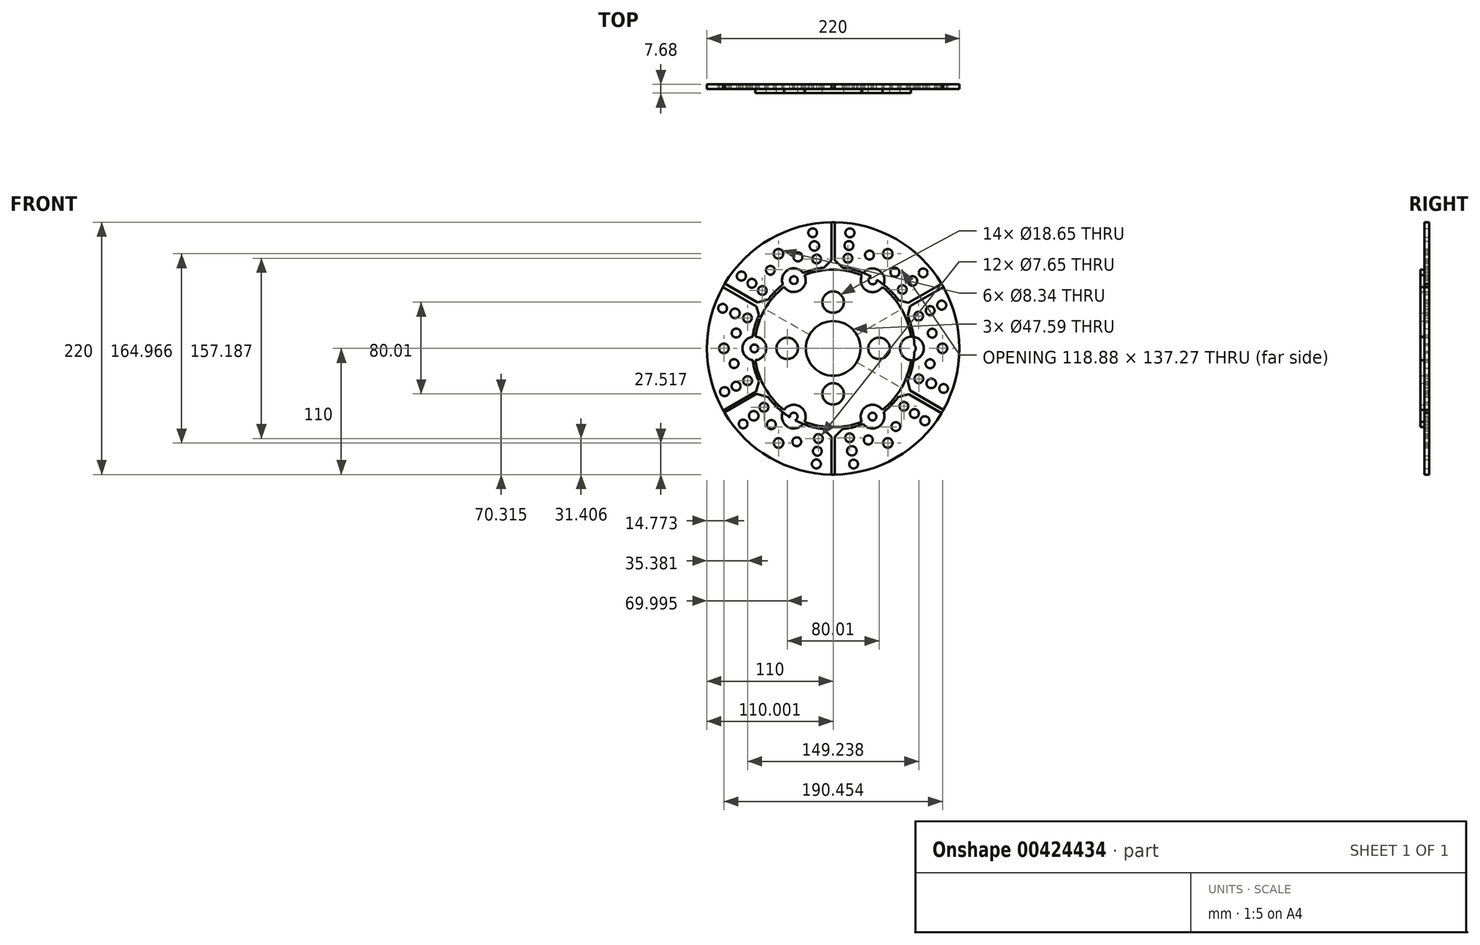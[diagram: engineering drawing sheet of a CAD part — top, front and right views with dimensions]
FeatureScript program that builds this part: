
annotation { "Feature Type Name" : "Feature", "Feature Type Description" : "" }
export const myFeature = defineFeature(function(context is Context, id is Id, definition is map)
    precondition{}
    {
        {
            var Q0;
            Q0=qCreatedBy(makeId("Front.planeOp"),FACE);
            var sketch = newSketch(context, id + "F0", { "sketchPlane" : qUnion([Q0])});
            skCircle(sketch, "E0", {"center": v(0, 0) * mm, "radius": 110 * mm});
            skLineSegment(sketch, "E1", {"start": v(0, 0) * mm, "end": v(0, -110) * mm});
            skLineSegment(sketch, "E2", {"start": v(0, 0) * mm, "end": v(0, 110) * mm});
            skLineSegment(sketch, "E3", {"start": v(0, 0) * mm, "end": v(95.26, 55) * mm});
            skLineSegment(sketch, "E4", {"start": v(0, 0) * mm, "end": v(95.27, -55) * mm});
            skLineSegment(sketch, "E5", {"start": v(0, 0) * mm, "end": v(-95.26, 55) * mm});
            skLineSegment(sketch, "E6", {"start": v(0, 0) * mm, "end": v(-95.26, -55) * mm});
            skCircle(sketch, "E7", {"center": v(0, 0) * mm, "radius": 68.64 * mm});
            skLineSegment(sketch, "E8", {"start": v(-10.54, 67.82) * mm, "end": v(0, 78.36) * mm});
            skLineSegment(sketch, "E9", {"start": v(0, 78.36) * mm, "end": v(10.54, 67.82) * mm});
            skLineSegment(sketch, "E10", {"start": v(10.7, -67.8) * mm, "end": v(-0.08, -78.58) * mm});
            skLineSegment(sketch, "E11", {"start": v(-0.08, -78.58) * mm, "end": v(-10.9, -67.77) * mm});
            skLineSegment(sketch, "E12", {"start": v(53.47, 43.04) * mm, "end": v(67.87, 39.18) * mm});
            skLineSegment(sketch, "E13", {"start": v(67.87, 39.18) * mm, "end": v(64, 24.78) * mm});
            skLineSegment(sketch, "E14", {"start": v(63.9, -25.04) * mm, "end": v(67.76, -39.44) * mm});
            skLineSegment(sketch, "E15", {"start": v(67.76, -39.44) * mm, "end": v(53.36, -43.3) * mm});
            skLineSegment(sketch, "E16", {"start": v(-53.24, -43.32) * mm, "end": v(-67.64, -39.46) * mm});
            skLineSegment(sketch, "E17", {"start": v(-67.64, -39.46) * mm, "end": v(-63.78, -25.06) * mm});
            skLineSegment(sketch, "E18", {"start": v(-63.8, 25.32) * mm, "end": v(-67.65, 39.72) * mm});
            skLineSegment(sketch, "E19", {"start": v(-67.65, 39.72) * mm, "end": v(-53.25, 43.58) * mm});
            skCircle(sketch, "E20", {"center": v(34.43, 59.38) * mm, "radius": 10.31 * mm});
            skCircle(sketch, "E21", {"center": v(-34.23, 59.49) * mm, "radius": 10.31 * mm});
            skCircle(sketch, "E22", {"center": v(68.64, 0) * mm, "radius": 10.31 * mm});
            skCircle(sketch, "E23", {"center": v(-68.64, 0) * mm, "radius": 10.31 * mm});
            skCircle(sketch, "E24", {"center": v(-34.32, -59.44) * mm, "radius": 10.31 * mm});
            skCircle(sketch, "E25", {"center": v(34.32, -59.44) * mm, "radius": 10.31 * mm});
            skLineSegment(sketch, "E26", {"start": v(-1.37, 110) * mm, "end": v(-1.37, 77) * mm});
            skLineSegment(sketch, "E27", {"start": v(1.46, 110) * mm, "end": v(1.46, 76.9) * mm});
            skLineSegment(sketch, "E28", {"start": v(96.08, 53.56) * mm, "end": v(67.26, 36.92) * mm});
            skLineSegment(sketch, "E29", {"start": v(94.44, 56.4) * mm, "end": v(65.65, 39.77) * mm});
            skLineSegment(sketch, "E30", {"start": v(94.47, -56.35) * mm, "end": v(66, -39.91) * mm});
            skLineSegment(sketch, "E31", {"start": v(96.12, -53.5) * mm, "end": v(67.03, -36.7) * mm});
            skLineSegment(sketch, "E32", {"start": v(-1.44, -77.22) * mm, "end": v(-1.44, -110) * mm});
            skLineSegment(sketch, "E33", {"start": v(1.34, -77.16) * mm, "end": v(1.34, -110) * mm});
            skLineSegment(sketch, "E34", {"start": v(-95.7, -54.25) * mm, "end": v(-67.2, -37.79) * mm});
            skLineSegment(sketch, "E35", {"start": v(-94.77, -55.84) * mm, "end": v(-66.8, -39.69) * mm});
            skLineSegment(sketch, "E36", {"start": v(-96.07, 53.58) * mm, "end": v(-66.84, 36.7) * mm});
            skLineSegment(sketch, "E37", {"start": v(-94.38, 56.5) * mm, "end": v(-66.05, 40.15) * mm});
            skCircle(sketch, "E38", {"center": v(0, 40.32) * mm, "radius": 9.33 * mm});
            skCircle(sketch, "E39", {"center": v(0, -39.69) * mm, "radius": 9.33 * mm});
            skCircle(sketch, "E40", {"center": v(40, 0) * mm, "radius": 9.33 * mm});
            skCircle(sketch, "E41", {"center": v(-40, 0) * mm, "radius": 9.33 * mm});
            skCircle(sketch, "E42", {"center": v(0, 0) * mm, "radius": 70.86 * mm});
            skCircle(sketch, "E43", {"center": v(0, 0) * mm, "radius": 23.8 * mm});
            skCircle(sketch, "E44", {"center": v(-34.23, 59.49) * mm, "radius": 3.38 * mm});
            skCircle(sketch, "E45", {"center": v(34.43, 59.38) * mm, "radius": 3.55 * mm});
            skCircle(sketch, "E46", {"center": v(68.64, 0) * mm, "radius": 3.38 * mm});
            skCircle(sketch, "E47", {"center": v(-34.32, -59.44) * mm, "radius": 3.38 * mm});
            skCircle(sketch, "E48", {"center": v(-68.64, 0) * mm, "radius": 3.38 * mm});
            skCircle(sketch, "E49", {"center": v(34.32, -59.44) * mm, "radius": 3.38 * mm});
            skCircle(sketch, "E50", {"center": v(-79.94, 63.04) * mm, "radius": 3.93 * mm});
            skCircle(sketch, "E51", {"center": v(-70.79, 56.73) * mm, "radius": 3.86 * mm});
            skCircle(sketch, "E52", {"center": v(-61.64, 50.43) * mm, "radius": 3.82 * mm});
            skCircle(sketch, "E53", {"center": v(-14.33, 77.89) * mm, "radius": 3.82 * mm});
            skCircle(sketch, "E54", {"center": v(-16.3, 89.3) * mm, "radius": 4.14 * mm});
            skCircle(sketch, "E55", {"center": v(-17.83, 100.85) * mm, "radius": 3.82 * mm});
            skCircle(sketch, "E56", {"center": v(-47.64, 82.46) * mm, "radius": 4.17 * mm});
            skCircle(sketch, "E57", {"center": v(-30.62, 79.8) * mm, "radius": 3.9 * mm});
            skCircle(sketch, "E58", {"center": v(-54.64, 68.13) * mm, "radius": 3.85 * mm});
            skCircle(sketch, "E59.1.0", {"center": v(-74.62, 26.53) * mm, "radius": 3.82 * mm});
            skCircle(sketch, "E59.1.1", {"center": v(-85.48, 30.53) * mm, "radius": 4.14 * mm});
            skCircle(sketch, "E59.1.2", {"center": v(-84.42, 13.38) * mm, "radius": 3.9 * mm});
            skCircle(sketch, "E59.1.3", {"center": v(-84.53, -32.94) * mm, "radius": 3.86 * mm});
            skCircle(sketch, "E59.1.4", {"center": v(-74.49, -28.17) * mm, "radius": 3.82 * mm});
            skCircle(sketch, "E59.1.5", {"center": v(-95.23, -0.03) * mm, "radius": 4.17 * mm});
            skCircle(sketch, "E59.1.6", {"center": v(-96.25, 34.98) * mm, "radius": 3.82 * mm});
            skCircle(sketch, "E59.1.7", {"center": v(-94.57, -37.7) * mm, "radius": 3.93 * mm});
            skCircle(sketch, "E59.1.8", {"center": v(-86.32, -13.25) * mm, "radius": 3.85 * mm});
            skCircle(sketch, "E59.2.0", {"center": v(-60.28, -51.36) * mm, "radius": 3.82 * mm});
            skCircle(sketch, "E59.2.1", {"center": v(-69.18, -58.76) * mm, "radius": 4.14 * mm});
            skCircle(sketch, "E59.2.2", {"center": v(-53.8, -66.42) * mm, "radius": 3.9 * mm});
            skCircle(sketch, "E59.2.3", {"center": v(-13.74, -89.67) * mm, "radius": 3.86 * mm});
            skCircle(sketch, "E59.2.4", {"center": v(-12.85, -78.6) * mm, "radius": 3.82 * mm});
            skCircle(sketch, "E59.2.5", {"center": v(-47.59, -82.48) * mm, "radius": 4.17 * mm});
            skCircle(sketch, "E59.2.6", {"center": v(-78.42, -65.87) * mm, "radius": 3.82 * mm});
            skCircle(sketch, "E59.2.7", {"center": v(-14.63, -100.75) * mm, "radius": 3.93 * mm});
            skCircle(sketch, "E59.2.8", {"center": v(-31.69, -81.38) * mm, "radius": 3.85 * mm});
            skCircle(sketch, "E59.3.0", {"center": v(14.33, -77.89) * mm, "radius": 3.82 * mm});
            skCircle(sketch, "E59.3.1", {"center": v(16.3, -89.3) * mm, "radius": 4.14 * mm});
            skCircle(sketch, "E59.3.2", {"center": v(30.62, -79.8) * mm, "radius": 3.9 * mm});
            skCircle(sketch, "E59.3.3", {"center": v(70.79, -56.73) * mm, "radius": 3.86 * mm});
            skCircle(sketch, "E59.3.4", {"center": v(61.64, -50.43) * mm, "radius": 3.82 * mm});
            skCircle(sketch, "E59.3.5", {"center": v(47.64, -82.46) * mm, "radius": 4.17 * mm});
            skCircle(sketch, "E59.3.6", {"center": v(17.83, -100.85) * mm, "radius": 3.82 * mm});
            skCircle(sketch, "E59.3.7", {"center": v(79.94, -63.04) * mm, "radius": 3.93 * mm});
            skCircle(sketch, "E59.3.8", {"center": v(54.64, -68.13) * mm, "radius": 3.85 * mm});
            skCircle(sketch, "E59.4.0", {"center": v(74.62, -26.53) * mm, "radius": 3.82 * mm});
            skCircle(sketch, "E59.4.1", {"center": v(85.48, -30.53) * mm, "radius": 4.14 * mm});
            skCircle(sketch, "E59.4.2", {"center": v(84.42, -13.38) * mm, "radius": 3.9 * mm});
            skCircle(sketch, "E59.4.3", {"center": v(84.53, 32.94) * mm, "radius": 3.86 * mm});
            skCircle(sketch, "E59.4.4", {"center": v(74.49, 28.17) * mm, "radius": 3.82 * mm});
            skCircle(sketch, "E59.4.5", {"center": v(95.23, 0.03) * mm, "radius": 4.17 * mm});
            skCircle(sketch, "E59.4.6", {"center": v(96.25, -34.98) * mm, "radius": 3.82 * mm});
            skCircle(sketch, "E59.4.7", {"center": v(94.57, 37.7) * mm, "radius": 3.93 * mm});
            skCircle(sketch, "E59.4.8", {"center": v(86.32, 13.25) * mm, "radius": 3.85 * mm});
            skCircle(sketch, "E59.5.0", {"center": v(60.28, 51.36) * mm, "radius": 3.82 * mm});
            skCircle(sketch, "E59.5.1", {"center": v(69.18, 58.76) * mm, "radius": 4.14 * mm});
            skCircle(sketch, "E59.5.2", {"center": v(53.8, 66.42) * mm, "radius": 3.9 * mm});
            skCircle(sketch, "E59.5.3", {"center": v(13.74, 89.67) * mm, "radius": 3.86 * mm});
            skCircle(sketch, "E59.5.4", {"center": v(12.85, 78.6) * mm, "radius": 3.82 * mm});
            skCircle(sketch, "E59.5.5", {"center": v(47.59, 82.48) * mm, "radius": 4.17 * mm});
            skCircle(sketch, "E59.5.6", {"center": v(78.42, 65.87) * mm, "radius": 3.82 * mm});
            skCircle(sketch, "E59.5.7", {"center": v(14.63, 100.75) * mm, "radius": 3.93 * mm});
            skCircle(sketch, "E59.5.8", {"center": v(31.69, 81.38) * mm, "radius": 3.85 * mm});
            skSolve(sketch);
        }
        {
            var Q0;
            {var subQ9=sQuery(id+"F0.wireOp",EDGE,"E26");Q0=makeQuery(id+"F0.imprint","IMPRINT",FACE,{"disambiguationData":[TD([[makeQuery(id+"F0.imprint","IMPRINT",EDGE,{"derivedFrom":subQ9}),-1.0]])]});}
            var Q1;
            {var subQ7=sQuery(id+"F0.wireOp",EDGE,"E27");Q1=makeQuery(id+"F0.imprint","IMPRINT",FACE,{"disambiguationData":[TD([[makeQuery(id+"F0.imprint","IMPRINT",EDGE,{"derivedFrom":subQ7}),1.0]])]});}
            var Q2;
            {var subQ7=sQuery(id+"F0.wireOp",EDGE,"E28");Q2=makeQuery(id+"F0.imprint","IMPRINT",FACE,{"disambiguationData":[TD([[makeQuery(id+"F0.imprint","IMPRINT",EDGE,{"derivedFrom":subQ7}),1.0]])]});}
            var Q3;
            {var subQ6=sQuery(id+"F0.wireOp",EDGE,"E30");Q3=makeQuery(id+"F0.imprint","IMPRINT",FACE,{"disambiguationData":[TD([[makeQuery(id+"F0.imprint","IMPRINT",EDGE,{"derivedFrom":subQ6}),1.0]])]});}
            var Q4;
            {var subQ7=sQuery(id+"F0.wireOp",EDGE,"E32");Q4=makeQuery(id+"F0.imprint","IMPRINT",FACE,{"disambiguationData":[TD([[makeQuery(id+"F0.imprint","IMPRINT",EDGE,{"derivedFrom":subQ7}),-1.0]])]});}
            var Q5;
            {var subQ7=sQuery(id+"F0.wireOp",EDGE,"E34");Q5=makeQuery(id+"F0.imprint","IMPRINT",FACE,{"disambiguationData":[TD([[makeQuery(id+"F0.imprint","IMPRINT",EDGE,{"derivedFrom":subQ7}),1.0]])]});}
            var Q6;
            {var subQ0=sQuery(id+"F0.wireOp",EDGE,"E43");var subQ9=sQuery(id+"F0.wireOp",EDGE,"E2");var subQ13=makeQuery(id+"F0.imprint","INTERSECT",VERTEX,{"derivedFrom":[subQ9,subQ0]});Q6=makeQuery(id+"F0.imprint","IMPRINT",FACE,{"disambiguationData":[TD([[makeQuery(id+"F0.imprint","IMPRINT",EDGE,{"disambiguationData":[TD([[subQ13,-1.0]])],"derivedFrom":subQ9}),1.0]])]});}
            var Q7;
            {var subQ4=sQuery(id+"F0.wireOp",EDGE,"E43");var subQ9=sQuery(id+"F0.wireOp",EDGE,"E2");var subQ12=makeQuery(id+"F0.imprint","INTERSECT",VERTEX,{"derivedFrom":[subQ9,subQ4]});Q7=makeQuery(id+"F0.imprint","IMPRINT",FACE,{"disambiguationData":[TD([[makeQuery(id+"F0.imprint","IMPRINT",EDGE,{"disambiguationData":[TD([[subQ12,-1.0]])],"derivedFrom":subQ9}),-1.0]])]});}
            var Q8;
            Q8=makeQuery(id+"F0.imprint","IMPRINT",FACE,{"disambiguationData":[TD([[makeQuery(id+"F0.imprint","IMPRINT",EDGE,{"derivedFrom":sQuery(id+"F0.wireOp",EDGE,"E41")}),-1.0]])]});
            var Q9;
            {var subQ0=sQuery(id+"F0.wireOp",EDGE,"E43");var subQ6=sQuery(id+"F0.wireOp",EDGE,"E1");var subQ11=makeQuery(id+"F0.imprint","INTERSECT",VERTEX,{"derivedFrom":[subQ6,subQ0]});Q9=makeQuery(id+"F0.imprint","IMPRINT",FACE,{"disambiguationData":[TD([[makeQuery(id+"F0.imprint","IMPRINT",EDGE,{"disambiguationData":[TD([[subQ11,-1.0]])],"derivedFrom":subQ6}),-1.0]])]});}
            var Q10;
            {var subQ0=sQuery(id+"F0.wireOp",EDGE,"E43");var subQ9=sQuery(id+"F0.wireOp",EDGE,"E1");var subQ13=makeQuery(id+"F0.imprint","INTERSECT",VERTEX,{"derivedFrom":[subQ9,subQ0]});Q10=makeQuery(id+"F0.imprint","IMPRINT",FACE,{"disambiguationData":[TD([[makeQuery(id+"F0.imprint","IMPRINT",EDGE,{"disambiguationData":[TD([[subQ13,-1.0]])],"derivedFrom":subQ9}),1.0]])]});}
            var Q11;
            Q11=makeQuery(id+"F0.imprint","IMPRINT",FACE,{"disambiguationData":[TD([[makeQuery(id+"F0.imprint","IMPRINT",EDGE,{"derivedFrom":sQuery(id+"F0.wireOp",EDGE,"E40")}),-1.0]])]});
            extrude(context, id + "F1", {"entities" : qUnion([Q0, Q1, Q2, Q3, Q4, Q5, Q6, Q7, Q8, Q9, Q10, Q11]), "depth" : 4 * mm});
        }
        {
            var Q0;
            {var subQ3=sQuery(id+"F0.wireOp",EDGE,"E36");Q0=makeQuery(id+"F0.imprint","IMPRINT",FACE,{"disambiguationData":[TD([[makeQuery(id+"F0.imprint","IMPRINT",EDGE,{"derivedFrom":subQ3}),1.0]])]});}
            var Q1;
            {var subQ3=sQuery(id+"F0.wireOp",EDGE,"E37");Q1=makeQuery(id+"F0.imprint","IMPRINT",FACE,{"disambiguationData":[TD([[makeQuery(id+"F0.imprint","IMPRINT",EDGE,{"derivedFrom":subQ3}),-1.0]])]});}
            var Q2;
            {var subQ2=sQuery(id+"F0.wireOp",EDGE,"E42");var subQ6=sQuery(id+"F0.wireOp",EDGE,"E5");var subQ8=makeQuery(id+"F0.imprint","INTERSECT",VERTEX,{"derivedFrom":[subQ6,subQ2]});Q2=makeQuery(id+"F0.imprint","IMPRINT",FACE,{"disambiguationData":[TD([[makeQuery(id+"F0.imprint","IMPRINT",EDGE,{"disambiguationData":[TD([[subQ8,-1.0]])],"derivedFrom":subQ6}),-1.0]])]});}
            var Q3;
            {var subQ0=sQuery(id+"F0.wireOp",EDGE,"E42");var subQ1=sQuery(id+"F0.wireOp",EDGE,"E5");var subQ2=makeQuery(id+"F0.imprint","INTERSECT",VERTEX,{"derivedFrom":[subQ1,subQ0]});Q3=makeQuery(id+"F0.imprint","IMPRINT",FACE,{"disambiguationData":[TD([[makeQuery(id+"F0.imprint","IMPRINT",EDGE,{"disambiguationData":[TD([[subQ2,-1.0]])],"derivedFrom":subQ1}),1.0]])]});}
            var Q4;
            {var subQ1=sQuery(id+"F0.wireOp",EDGE,"E7");var subQ6=sQuery(id+"F0.wireOp",EDGE,"E5");var subQ7=makeQuery(id+"F0.imprint","INTERSECT",VERTEX,{"derivedFrom":[subQ6,subQ1]});Q4=makeQuery(id+"F0.imprint","IMPRINT",FACE,{"disambiguationData":[TD([[makeQuery(id+"F0.imprint","IMPRINT",EDGE,{"disambiguationData":[TD([[subQ7,-1.0]])],"derivedFrom":subQ6}),-1.0]])]});}
            var Q5;
            {var subQ0=sQuery(id+"F0.wireOp",EDGE,"E7");var subQ1=sQuery(id+"F0.wireOp",EDGE,"E5");var subQ2=makeQuery(id+"F0.imprint","INTERSECT",VERTEX,{"derivedFrom":[subQ1,subQ0]});Q5=makeQuery(id+"F0.imprint","IMPRINT",FACE,{"disambiguationData":[TD([[makeQuery(id+"F0.imprint","IMPRINT",EDGE,{"disambiguationData":[TD([[subQ2,-1.0]])],"derivedFrom":subQ1}),1.0]])]});}
            var Q6;
            {var subQ0=sQuery(id+"F0.wireOp",EDGE,"E18");var subQ1=sQuery(id+"F0.wireOp",EDGE,"E7");var subQ2=makeQuery(id+"F0.imprint","INTERSECT",VERTEX,{"derivedFrom":[subQ1,subQ0]});Q6=makeQuery(id+"F0.imprint","IMPRINT",FACE,{"disambiguationData":[TD([[makeQuery(id+"F0.imprint","IMPRINT",EDGE,{"disambiguationData":[TD([[subQ2,-1.0]])],"derivedFrom":subQ1}),-1.0]])]});}
            var Q7;
            {var subQ0=sQuery(id+"F0.wireOp",EDGE,"E23");var subQ1=sQuery(id+"F0.wireOp",EDGE,"E7");var subQ2=makeQuery(id+"F0.imprint","INTERSECT",VERTEX,{"disambiguationData":[OD(0.0)],"derivedFrom":[subQ1,subQ0]});Q7=makeQuery(id+"F0.imprint","IMPRINT",FACE,{"disambiguationData":[TD([[makeQuery(id+"F0.imprint","IMPRINT",EDGE,{"disambiguationData":[TD([[subQ2,-1.0]])],"derivedFrom":subQ1}),-1.0]])]});}
            var Q8;
            {var subQ0=sQuery(id+"F0.wireOp",EDGE,"E42");var subQ1=sQuery(id+"F0.wireOp",EDGE,"E23");var subQ2=makeQuery(id+"F0.imprint","INTERSECT",VERTEX,{"disambiguationData":[OD(0.0)],"derivedFrom":[subQ1,subQ0]});Q8=makeQuery(id+"F0.imprint","IMPRINT",FACE,{"disambiguationData":[TD([[makeQuery(id+"F0.imprint","IMPRINT",EDGE,{"disambiguationData":[TD([[subQ2,-1.0]])],"derivedFrom":subQ1}),1.0]])]});}
            var Q9;
            {var subQ0=sQuery(id+"F0.wireOp",EDGE,"E23");var subQ1=sQuery(id+"F0.wireOp",EDGE,"E7");var subQ2=makeQuery(id+"F0.imprint","INTERSECT",VERTEX,{"disambiguationData":[OD(0.0)],"derivedFrom":[subQ1,subQ0]});Q9=makeQuery(id+"F0.imprint","IMPRINT",FACE,{"disambiguationData":[TD([[makeQuery(id+"F0.imprint","IMPRINT",EDGE,{"disambiguationData":[TD([[subQ2,-1.0]])],"derivedFrom":subQ1}),1.0]])]});}
            var Q10;
            {var subQ0=sQuery(id+"F0.wireOp",EDGE,"E48");var subQ1=sQuery(id+"F0.wireOp",EDGE,"E7");var subQ2=makeQuery(id+"F0.imprint","INTERSECT",VERTEX,{"disambiguationData":[OD(1.0)],"derivedFrom":[subQ1,subQ0]});Q10=makeQuery(id+"F0.imprint","IMPRINT",FACE,{"disambiguationData":[TD([[makeQuery(id+"F0.imprint","IMPRINT",EDGE,{"disambiguationData":[TD([[subQ2,-1.0]])],"derivedFrom":subQ1}),-1.0]])]});}
            var Q11;
            {var subQ0=sQuery(id+"F0.wireOp",EDGE,"E17");var subQ1=sQuery(id+"F0.wireOp",EDGE,"E7");var subQ2=makeQuery(id+"F0.imprint","INTERSECT",VERTEX,{"derivedFrom":[subQ1,subQ0]});Q11=makeQuery(id+"F0.imprint","IMPRINT",FACE,{"disambiguationData":[TD([[makeQuery(id+"F0.imprint","IMPRINT",EDGE,{"disambiguationData":[TD([[subQ2,1.0]])],"derivedFrom":subQ1}),-1.0]])]});}
            var Q12;
            {var subQ0=sQuery(id+"F0.wireOp",EDGE,"E7");var subQ1=sQuery(id+"F0.wireOp",EDGE,"E6");var subQ2=makeQuery(id+"F0.imprint","INTERSECT",VERTEX,{"derivedFrom":[subQ1,subQ0]});Q12=makeQuery(id+"F0.imprint","IMPRINT",FACE,{"disambiguationData":[TD([[makeQuery(id+"F0.imprint","IMPRINT",EDGE,{"disambiguationData":[TD([[subQ2,-1.0]])],"derivedFrom":subQ1}),1.0]])]});}
            var Q13;
            {var subQ0=sQuery(id+"F0.wireOp",EDGE,"E7");var subQ1=sQuery(id+"F0.wireOp",EDGE,"E6");var subQ2=makeQuery(id+"F0.imprint","INTERSECT",VERTEX,{"derivedFrom":[subQ1,subQ0]});Q13=makeQuery(id+"F0.imprint","IMPRINT",FACE,{"disambiguationData":[TD([[makeQuery(id+"F0.imprint","IMPRINT",EDGE,{"disambiguationData":[TD([[subQ2,-1.0]])],"derivedFrom":subQ1}),-1.0]])]});}
            var Q14;
            {var subQ0=sQuery(id+"F0.wireOp",EDGE,"E42");var subQ1=sQuery(id+"F0.wireOp",EDGE,"E6");var subQ2=makeQuery(id+"F0.imprint","INTERSECT",VERTEX,{"derivedFrom":[subQ1,subQ0]});Q14=makeQuery(id+"F0.imprint","IMPRINT",FACE,{"disambiguationData":[TD([[makeQuery(id+"F0.imprint","IMPRINT",EDGE,{"disambiguationData":[TD([[subQ2,-1.0]])],"derivedFrom":subQ1}),-1.0]])]});}
            var Q15;
            {var subQ3=sQuery(id+"F0.wireOp",EDGE,"E6");var subQ6=sQuery(id+"F0.wireOp",EDGE,"E42");var subQ7=makeQuery(id+"F0.imprint","INTERSECT",VERTEX,{"derivedFrom":[subQ3,subQ6]});Q15=makeQuery(id+"F0.imprint","IMPRINT",FACE,{"disambiguationData":[TD([[makeQuery(id+"F0.imprint","IMPRINT",EDGE,{"disambiguationData":[TD([[subQ7,-1.0]])],"derivedFrom":subQ3}),1.0]])]});}
            var Q16;
            {var subQ3=sQuery(id+"F0.wireOp",EDGE,"E34");Q16=makeQuery(id+"F0.imprint","IMPRINT",FACE,{"disambiguationData":[TD([[makeQuery(id+"F0.imprint","IMPRINT",EDGE,{"derivedFrom":subQ3}),-1.0]])]});}
            var Q17;
            {var subQ5=sQuery(id+"F0.wireOp",EDGE,"E35");Q17=makeQuery(id+"F0.imprint","IMPRINT",FACE,{"disambiguationData":[TD([[makeQuery(id+"F0.imprint","IMPRINT",EDGE,{"derivedFrom":subQ5}),1.0]])]});}
            var Q18;
            Q18=makeQuery(id+"F1.opExtrude","CAP_FACE",FACE,{"disambiguationData":[OSD([sQuery(id+"F0.wireOp",EDGE,"E7"),sQuery(id+"F0.wireOp",EDGE,"E20"),sQuery(id+"F0.wireOp",EDGE,"E21"),sQuery(id+"F0.wireOp",EDGE,"E22"),sQuery(id+"F0.wireOp",EDGE,"E23"),sQuery(id+"F0.wireOp",EDGE,"E24"),sQuery(id+"F0.wireOp",EDGE,"E25"),sQuery(id+"F0.wireOp",EDGE,"E38"),sQuery(id+"F0.wireOp",EDGE,"E39"),sQuery(id+"F0.wireOp",EDGE,"E40"),sQuery(id+"F0.wireOp",EDGE,"E41"),sQuery(id+"F0.wireOp",EDGE,"E43")])],"isStart":false});
            var Q19;
            {var subQ0=sQuery(id+"F0.wireOp",EDGE,"E43");var subQ6=sQuery(id+"F0.wireOp",EDGE,"E1");var subQ10=makeQuery(id+"F0.imprint","INTERSECT",VERTEX,{"derivedFrom":[subQ6,subQ0]});Q19=makeQuery(id+"F0.imprint","IMPRINT",FACE,{"disambiguationData":[TD([[makeQuery(id+"F0.imprint","IMPRINT",EDGE,{"disambiguationData":[TD([[subQ10,-1.0]])],"derivedFrom":subQ6}),-1.0]])]});}
            var Q20;
            Q20=makeQuery(id+"F0.imprint","IMPRINT",FACE,{"disambiguationData":[TD([[makeQuery(id+"F0.imprint","IMPRINT",EDGE,{"derivedFrom":sQuery(id+"F0.wireOp",EDGE,"E41")}),-1.0]])]});
            var Q21;
            Q21=makeQuery(id+"F1.opExtrude","CAP_FACE",FACE,{"disambiguationData":[OSD([sQuery(id+"F0.wireOp",EDGE,"E7"),sQuery(id+"F0.wireOp",EDGE,"E20"),sQuery(id+"F0.wireOp",EDGE,"E21"),sQuery(id+"F0.wireOp",EDGE,"E22"),sQuery(id+"F0.wireOp",EDGE,"E23"),sQuery(id+"F0.wireOp",EDGE,"E24"),sQuery(id+"F0.wireOp",EDGE,"E25"),sQuery(id+"F0.wireOp",EDGE,"E38"),sQuery(id+"F0.wireOp",EDGE,"E39"),sQuery(id+"F0.wireOp",EDGE,"E40"),sQuery(id+"F0.wireOp",EDGE,"E41"),sQuery(id+"F0.wireOp",EDGE,"E43")])],"isStart":true});
            var Q22;
            {var subQ0=sQuery(id+"F0.wireOp",EDGE,"E16");var subQ1=sQuery(id+"F0.wireOp",EDGE,"E7");var subQ2=makeQuery(id+"F0.imprint","INTERSECT",VERTEX,{"derivedFrom":[subQ1,subQ0]});Q22=makeQuery(id+"F0.imprint","IMPRINT",FACE,{"disambiguationData":[TD([[makeQuery(id+"F0.imprint","IMPRINT",EDGE,{"disambiguationData":[TD([[subQ2,-1.0]])],"derivedFrom":subQ1}),-1.0]])]});}
            var Q23;
            {var subQ0=sQuery(id+"F0.wireOp",EDGE,"E42");var subQ1=sQuery(id+"F0.wireOp",EDGE,"E24");var subQ2=makeQuery(id+"F0.imprint","INTERSECT",VERTEX,{"disambiguationData":[OD(0.0)],"derivedFrom":[subQ1,subQ0]});Q23=makeQuery(id+"F0.imprint","IMPRINT",FACE,{"disambiguationData":[TD([[makeQuery(id+"F0.imprint","IMPRINT",EDGE,{"disambiguationData":[TD([[subQ2,-1.0]])],"derivedFrom":subQ1}),1.0]])]});}
            var Q24;
            {var subQ0=sQuery(id+"F0.wireOp",EDGE,"E47");var subQ1=sQuery(id+"F0.wireOp",EDGE,"E7");var subQ2=makeQuery(id+"F0.imprint","INTERSECT",VERTEX,{"disambiguationData":[OD(1.0)],"derivedFrom":[subQ1,subQ0]});Q24=makeQuery(id+"F0.imprint","IMPRINT",FACE,{"disambiguationData":[TD([[makeQuery(id+"F0.imprint","IMPRINT",EDGE,{"disambiguationData":[TD([[subQ2,-1.0]])],"derivedFrom":subQ1}),-1.0]])]});}
            var Q25;
            {var subQ0=sQuery(id+"F0.wireOp",EDGE,"E24");var subQ1=sQuery(id+"F0.wireOp",EDGE,"E7");var subQ2=makeQuery(id+"F0.imprint","INTERSECT",VERTEX,{"disambiguationData":[OD(0.0)],"derivedFrom":[subQ1,subQ0]});Q25=makeQuery(id+"F0.imprint","IMPRINT",FACE,{"disambiguationData":[TD([[makeQuery(id+"F0.imprint","IMPRINT",EDGE,{"disambiguationData":[TD([[subQ2,-1.0]])],"derivedFrom":subQ1}),-1.0]])]});}
            var Q26;
            {var subQ0=sQuery(id+"F0.wireOp",EDGE,"E24");var subQ1=sQuery(id+"F0.wireOp",EDGE,"E7");var subQ2=makeQuery(id+"F0.imprint","INTERSECT",VERTEX,{"disambiguationData":[OD(0.0)],"derivedFrom":[subQ1,subQ0]});Q26=makeQuery(id+"F0.imprint","IMPRINT",FACE,{"disambiguationData":[TD([[makeQuery(id+"F0.imprint","IMPRINT",EDGE,{"disambiguationData":[TD([[subQ2,-1.0]])],"derivedFrom":subQ1}),1.0]])]});}
            var Q27;
            {var subQ0=sQuery(id+"F0.wireOp",EDGE,"E11");var subQ1=sQuery(id+"F0.wireOp",EDGE,"E7");var subQ2=makeQuery(id+"F0.imprint","INTERSECT",VERTEX,{"derivedFrom":[subQ1,subQ0]});Q27=makeQuery(id+"F0.imprint","IMPRINT",FACE,{"disambiguationData":[TD([[makeQuery(id+"F0.imprint","IMPRINT",EDGE,{"disambiguationData":[TD([[subQ2,1.0]])],"derivedFrom":subQ1}),-1.0]])]});}
            var Q28;
            {var subQ2=sQuery(id+"F0.wireOp",EDGE,"E42");var subQ4=sQuery(id+"F0.wireOp",EDGE,"E1");var subQ5=makeQuery(id+"F0.imprint","INTERSECT",VERTEX,{"derivedFrom":[subQ4,subQ2]});Q28=makeQuery(id+"F0.imprint","IMPRINT",FACE,{"disambiguationData":[TD([[makeQuery(id+"F0.imprint","IMPRINT",EDGE,{"disambiguationData":[TD([[subQ5,-1.0]])],"derivedFrom":subQ4}),-1.0]])]});}
            var Q29;
            {var subQ0=sQuery(id+"F0.wireOp",EDGE,"E42");var subQ1=sQuery(id+"F0.wireOp",EDGE,"E1");var subQ2=makeQuery(id+"F0.imprint","INTERSECT",VERTEX,{"derivedFrom":[subQ1,subQ0]});Q29=makeQuery(id+"F0.imprint","IMPRINT",FACE,{"disambiguationData":[TD([[makeQuery(id+"F0.imprint","IMPRINT",EDGE,{"disambiguationData":[TD([[subQ2,-1.0]])],"derivedFrom":subQ1}),1.0]])]});}
            var Q30;
            {var subQ0=sQuery(id+"F0.wireOp",EDGE,"E7");var subQ1=sQuery(id+"F0.wireOp",EDGE,"E1");var subQ2=makeQuery(id+"F0.imprint","INTERSECT",VERTEX,{"derivedFrom":[subQ1,subQ0]});Q30=makeQuery(id+"F0.imprint","IMPRINT",FACE,{"disambiguationData":[TD([[makeQuery(id+"F0.imprint","IMPRINT",EDGE,{"disambiguationData":[TD([[subQ2,-1.0]])],"derivedFrom":subQ1}),1.0]])]});}
            var Q31;
            {var subQ0=sQuery(id+"F0.wireOp",EDGE,"E7");var subQ1=sQuery(id+"F0.wireOp",EDGE,"E1");var subQ2=makeQuery(id+"F0.imprint","INTERSECT",VERTEX,{"derivedFrom":[subQ1,subQ0]});Q31=makeQuery(id+"F0.imprint","IMPRINT",FACE,{"disambiguationData":[TD([[makeQuery(id+"F0.imprint","IMPRINT",EDGE,{"disambiguationData":[TD([[subQ2,-1.0]])],"derivedFrom":subQ1}),-1.0]])]});}
            var Q32;
            {var subQ0=sQuery(id+"F0.wireOp",EDGE,"E10");var subQ1=sQuery(id+"F0.wireOp",EDGE,"E7");var subQ2=makeQuery(id+"F0.imprint","INTERSECT",VERTEX,{"derivedFrom":[subQ1,subQ0]});Q32=makeQuery(id+"F0.imprint","IMPRINT",FACE,{"disambiguationData":[TD([[makeQuery(id+"F0.imprint","IMPRINT",EDGE,{"disambiguationData":[TD([[subQ2,-1.0]])],"derivedFrom":subQ1}),-1.0]])]});}
            var Q33;
            {var subQ0=sQuery(id+"F0.wireOp",EDGE,"E42");var subQ1=sQuery(id+"F0.wireOp",EDGE,"E25");var subQ2=makeQuery(id+"F0.imprint","INTERSECT",VERTEX,{"disambiguationData":[OD(0.0)],"derivedFrom":[subQ1,subQ0]});Q33=makeQuery(id+"F0.imprint","IMPRINT",FACE,{"disambiguationData":[TD([[makeQuery(id+"F0.imprint","IMPRINT",EDGE,{"disambiguationData":[TD([[subQ2,1.0]])],"derivedFrom":subQ1}),1.0]])]});}
            var Q34;
            {var subQ0=sQuery(id+"F0.wireOp",EDGE,"E25");var subQ1=sQuery(id+"F0.wireOp",EDGE,"E7");var subQ2=makeQuery(id+"F0.imprint","INTERSECT",VERTEX,{"disambiguationData":[OD(0.0)],"derivedFrom":[subQ1,subQ0]});Q34=makeQuery(id+"F0.imprint","IMPRINT",FACE,{"disambiguationData":[TD([[makeQuery(id+"F0.imprint","IMPRINT",EDGE,{"disambiguationData":[TD([[subQ2,-1.0]])],"derivedFrom":subQ1}),1.0]])]});}
            var Q35;
            {var subQ0=sQuery(id+"F0.wireOp",EDGE,"E25");var subQ1=sQuery(id+"F0.wireOp",EDGE,"E7");var subQ2=makeQuery(id+"F0.imprint","INTERSECT",VERTEX,{"disambiguationData":[OD(0.0)],"derivedFrom":[subQ1,subQ0]});Q35=makeQuery(id+"F0.imprint","IMPRINT",FACE,{"disambiguationData":[TD([[makeQuery(id+"F0.imprint","IMPRINT",EDGE,{"disambiguationData":[TD([[subQ2,-1.0]])],"derivedFrom":subQ1}),-1.0]])]});}
            var Q36;
            {var subQ0=sQuery(id+"F0.wireOp",EDGE,"E49");var subQ1=sQuery(id+"F0.wireOp",EDGE,"E7");var subQ2=makeQuery(id+"F0.imprint","INTERSECT",VERTEX,{"disambiguationData":[OD(1.0)],"derivedFrom":[subQ1,subQ0]});Q36=makeQuery(id+"F0.imprint","IMPRINT",FACE,{"disambiguationData":[TD([[makeQuery(id+"F0.imprint","IMPRINT",EDGE,{"disambiguationData":[TD([[subQ2,-1.0]])],"derivedFrom":subQ1}),-1.0]])]});}
            var Q37;
            {var subQ4=sQuery(id+"F0.wireOp",EDGE,"E7");var subQ5=sQuery(id+"F0.wireOp",EDGE,"E4");var subQ6=makeQuery(id+"F0.imprint","INTERSECT",VERTEX,{"derivedFrom":[subQ5,subQ4]});Q37=makeQuery(id+"F0.imprint","IMPRINT",FACE,{"disambiguationData":[TD([[makeQuery(id+"F0.imprint","IMPRINT",EDGE,{"disambiguationData":[TD([[subQ6,-1.0]])],"derivedFrom":subQ5}),-1.0]])]});}
            var Q38;
            {var subQ4=sQuery(id+"F0.wireOp",EDGE,"E4");var subQ6=sQuery(id+"F0.wireOp",EDGE,"E42");var subQ8=makeQuery(id+"F0.imprint","INTERSECT",VERTEX,{"derivedFrom":[subQ4,subQ6]});Q38=makeQuery(id+"F0.imprint","IMPRINT",FACE,{"disambiguationData":[TD([[makeQuery(id+"F0.imprint","IMPRINT",EDGE,{"disambiguationData":[TD([[subQ8,-1.0]])],"derivedFrom":subQ4}),-1.0]])]});}
            var Q39;
            {var subQ0=sQuery(id+"F0.wireOp",EDGE,"E42");var subQ1=sQuery(id+"F0.wireOp",EDGE,"E4");var subQ2=makeQuery(id+"F0.imprint","INTERSECT",VERTEX,{"derivedFrom":[subQ1,subQ0]});Q39=makeQuery(id+"F0.imprint","IMPRINT",FACE,{"disambiguationData":[TD([[makeQuery(id+"F0.imprint","IMPRINT",EDGE,{"disambiguationData":[TD([[subQ2,-1.0]])],"derivedFrom":subQ1}),1.0]])]});}
            var Q40;
            {var subQ3=sQuery(id+"F0.wireOp",EDGE,"E30");Q40=makeQuery(id+"F0.imprint","IMPRINT",FACE,{"disambiguationData":[TD([[makeQuery(id+"F0.imprint","IMPRINT",EDGE,{"derivedFrom":subQ3}),-1.0]])]});}
            var Q41;
            {var subQ3=sQuery(id+"F0.wireOp",EDGE,"E31");Q41=makeQuery(id+"F0.imprint","IMPRINT",FACE,{"disambiguationData":[TD([[makeQuery(id+"F0.imprint","IMPRINT",EDGE,{"derivedFrom":subQ3}),1.0]])]});}
            var Q42;
            {var subQ0=sQuery(id+"F0.wireOp",EDGE,"E7");var subQ1=sQuery(id+"F0.wireOp",EDGE,"E4");var subQ2=makeQuery(id+"F0.imprint","INTERSECT",VERTEX,{"derivedFrom":[subQ1,subQ0]});Q42=makeQuery(id+"F0.imprint","IMPRINT",FACE,{"disambiguationData":[TD([[makeQuery(id+"F0.imprint","IMPRINT",EDGE,{"disambiguationData":[TD([[subQ2,-1.0]])],"derivedFrom":subQ1}),1.0]])]});}
            var Q43;
            {var subQ0=sQuery(id+"F0.wireOp",EDGE,"E14");var subQ1=sQuery(id+"F0.wireOp",EDGE,"E7");var subQ2=makeQuery(id+"F0.imprint","INTERSECT",VERTEX,{"derivedFrom":[subQ1,subQ0]});Q43=makeQuery(id+"F0.imprint","IMPRINT",FACE,{"disambiguationData":[TD([[makeQuery(id+"F0.imprint","IMPRINT",EDGE,{"disambiguationData":[TD([[subQ2,-1.0]])],"derivedFrom":subQ1}),-1.0]])]});}
            var Q44;
            {var subQ0=sQuery(id+"F0.wireOp",EDGE,"E22");var subQ1=sQuery(id+"F0.wireOp",EDGE,"E7");var subQ2=makeQuery(id+"F0.imprint","INTERSECT",VERTEX,{"disambiguationData":[OD(1.0)],"derivedFrom":[subQ1,subQ0]});Q44=makeQuery(id+"F0.imprint","IMPRINT",FACE,{"disambiguationData":[TD([[makeQuery(id+"F0.imprint","IMPRINT",EDGE,{"disambiguationData":[TD([[subQ2,-1.0]])],"derivedFrom":subQ1}),-1.0]])]});}
            var Q45;
            {var subQ0=sQuery(id+"F0.wireOp",EDGE,"E22");var subQ1=sQuery(id+"F0.wireOp",EDGE,"E7");var subQ2=makeQuery(id+"F0.imprint","INTERSECT",VERTEX,{"disambiguationData":[OD(0.0)],"derivedFrom":[subQ1,subQ0]});Q45=makeQuery(id+"F0.imprint","IMPRINT",FACE,{"disambiguationData":[TD([[makeQuery(id+"F0.imprint","IMPRINT",EDGE,{"disambiguationData":[TD([[subQ2,1.0]])],"derivedFrom":subQ1}),1.0]])]});}
            var Q46;
            {var subQ0=sQuery(id+"F0.wireOp",EDGE,"E42");var subQ1=sQuery(id+"F0.wireOp",EDGE,"E22");var subQ2=makeQuery(id+"F0.imprint","INTERSECT",VERTEX,{"disambiguationData":[OD(0.0)],"derivedFrom":[subQ1,subQ0]});Q46=makeQuery(id+"F0.imprint","IMPRINT",FACE,{"disambiguationData":[TD([[makeQuery(id+"F0.imprint","IMPRINT",EDGE,{"disambiguationData":[TD([[subQ2,1.0]])],"derivedFrom":subQ1}),1.0]])]});}
            var Q47;
            {var subQ0=sQuery(id+"F0.wireOp",EDGE,"E22");var subQ1=sQuery(id+"F0.wireOp",EDGE,"E7");var subQ2=makeQuery(id+"F0.imprint","INTERSECT",VERTEX,{"disambiguationData":[OD(0.0)],"derivedFrom":[subQ1,subQ0]});Q47=makeQuery(id+"F0.imprint","IMPRINT",FACE,{"disambiguationData":[TD([[makeQuery(id+"F0.imprint","IMPRINT",EDGE,{"disambiguationData":[TD([[subQ2,1.0]])],"derivedFrom":subQ1}),-1.0]])]});}
            var Q48;
            {var subQ2=sQuery(id+"F0.wireOp",EDGE,"E42");var subQ6=sQuery(id+"F0.wireOp",EDGE,"E3");var subQ8=makeQuery(id+"F0.imprint","INTERSECT",VERTEX,{"derivedFrom":[subQ6,subQ2]});Q48=makeQuery(id+"F0.imprint","IMPRINT",FACE,{"disambiguationData":[TD([[makeQuery(id+"F0.imprint","IMPRINT",EDGE,{"disambiguationData":[TD([[subQ8,-1.0]])],"derivedFrom":subQ6}),-1.0]])]});}
            var Q49;
            {var subQ0=sQuery(id+"F0.wireOp",EDGE,"E7");var subQ1=sQuery(id+"F0.wireOp",EDGE,"E3");var subQ2=makeQuery(id+"F0.imprint","INTERSECT",VERTEX,{"derivedFrom":[subQ1,subQ0]});Q49=makeQuery(id+"F0.imprint","IMPRINT",FACE,{"disambiguationData":[TD([[makeQuery(id+"F0.imprint","IMPRINT",EDGE,{"disambiguationData":[TD([[subQ2,-1.0]])],"derivedFrom":subQ1}),1.0]])]});}
            var Q50;
            {var subQ0=sQuery(id+"F0.wireOp",EDGE,"E42");var subQ1=sQuery(id+"F0.wireOp",EDGE,"E3");var subQ2=makeQuery(id+"F0.imprint","INTERSECT",VERTEX,{"derivedFrom":[subQ1,subQ0]});Q50=makeQuery(id+"F0.imprint","IMPRINT",FACE,{"disambiguationData":[TD([[makeQuery(id+"F0.imprint","IMPRINT",EDGE,{"disambiguationData":[TD([[subQ2,-1.0]])],"derivedFrom":subQ1}),1.0]])]});}
            var Q51;
            {var subQ4=sQuery(id+"F0.wireOp",EDGE,"E7");var subQ6=sQuery(id+"F0.wireOp",EDGE,"E3");var subQ7=makeQuery(id+"F0.imprint","INTERSECT",VERTEX,{"derivedFrom":[subQ6,subQ4]});Q51=makeQuery(id+"F0.imprint","IMPRINT",FACE,{"disambiguationData":[TD([[makeQuery(id+"F0.imprint","IMPRINT",EDGE,{"disambiguationData":[TD([[subQ7,-1.0]])],"derivedFrom":subQ6}),-1.0]])]});}
            var Q52;
            {var subQ3=sQuery(id+"F0.wireOp",EDGE,"E28");Q52=makeQuery(id+"F0.imprint","IMPRINT",FACE,{"disambiguationData":[TD([[makeQuery(id+"F0.imprint","IMPRINT",EDGE,{"derivedFrom":subQ3}),-1.0]])]});}
            var Q53;
            {var subQ3=sQuery(id+"F0.wireOp",EDGE,"E29");Q53=makeQuery(id+"F0.imprint","IMPRINT",FACE,{"disambiguationData":[TD([[makeQuery(id+"F0.imprint","IMPRINT",EDGE,{"derivedFrom":subQ3}),1.0]])]});}
            var Q54;
            {var subQ0=sQuery(id+"F0.wireOp",EDGE,"E12");var subQ1=sQuery(id+"F0.wireOp",EDGE,"E7");var subQ2=makeQuery(id+"F0.imprint","INTERSECT",VERTEX,{"derivedFrom":[subQ1,subQ0]});Q54=makeQuery(id+"F0.imprint","IMPRINT",FACE,{"disambiguationData":[TD([[makeQuery(id+"F0.imprint","IMPRINT",EDGE,{"disambiguationData":[TD([[subQ2,-1.0]])],"derivedFrom":subQ1}),-1.0]])]});}
            var Q55;
            {var subQ0=sQuery(id+"F0.wireOp",EDGE,"E20");var subQ1=sQuery(id+"F0.wireOp",EDGE,"E7");var subQ2=makeQuery(id+"F0.imprint","INTERSECT",VERTEX,{"disambiguationData":[OD(0.0)],"derivedFrom":[subQ1,subQ0]});Q55=makeQuery(id+"F0.imprint","IMPRINT",FACE,{"disambiguationData":[TD([[makeQuery(id+"F0.imprint","IMPRINT",EDGE,{"disambiguationData":[TD([[subQ2,-1.0]])],"derivedFrom":subQ1}),-1.0]])]});}
            var Q56;
            {var subQ0=sQuery(id+"F0.wireOp",EDGE,"E20");var subQ1=sQuery(id+"F0.wireOp",EDGE,"E7");var subQ2=makeQuery(id+"F0.imprint","INTERSECT",VERTEX,{"disambiguationData":[OD(0.0)],"derivedFrom":[subQ1,subQ0]});Q56=makeQuery(id+"F0.imprint","IMPRINT",FACE,{"disambiguationData":[TD([[makeQuery(id+"F0.imprint","IMPRINT",EDGE,{"disambiguationData":[TD([[subQ2,-1.0]])],"derivedFrom":subQ1}),1.0]])]});}
            var Q57;
            {var subQ0=sQuery(id+"F0.wireOp",EDGE,"E42");var subQ1=sQuery(id+"F0.wireOp",EDGE,"E20");var subQ2=makeQuery(id+"F0.imprint","INTERSECT",VERTEX,{"disambiguationData":[OD(0.0)],"derivedFrom":[subQ1,subQ0]});Q57=makeQuery(id+"F0.imprint","IMPRINT",FACE,{"disambiguationData":[TD([[makeQuery(id+"F0.imprint","IMPRINT",EDGE,{"disambiguationData":[TD([[subQ2,1.0]])],"derivedFrom":subQ1}),1.0]])]});}
            var Q58;
            {var subQ0=sQuery(id+"F0.wireOp",EDGE,"E45");var subQ1=sQuery(id+"F0.wireOp",EDGE,"E7");var subQ2=makeQuery(id+"F0.imprint","INTERSECT",VERTEX,{"disambiguationData":[OD(1.0)],"derivedFrom":[subQ1,subQ0]});Q58=makeQuery(id+"F0.imprint","IMPRINT",FACE,{"disambiguationData":[TD([[makeQuery(id+"F0.imprint","IMPRINT",EDGE,{"disambiguationData":[TD([[subQ2,-1.0]])],"derivedFrom":subQ1}),-1.0]])]});}
            var Q59;
            {var subQ3=sQuery(id+"F0.wireOp",EDGE,"E27");Q59=makeQuery(id+"F0.imprint","IMPRINT",FACE,{"disambiguationData":[TD([[makeQuery(id+"F0.imprint","IMPRINT",EDGE,{"derivedFrom":subQ3}),-1.0]])]});}
            var Q60;
            {var subQ3=sQuery(id+"F0.wireOp",EDGE,"E26");Q60=makeQuery(id+"F0.imprint","IMPRINT",FACE,{"disambiguationData":[TD([[makeQuery(id+"F0.imprint","IMPRINT",EDGE,{"derivedFrom":subQ3}),1.0]])]});}
            var Q61;
            {var subQ0=sQuery(id+"F0.wireOp",EDGE,"E9");var subQ5=makeQuery(id+"F0.imprint","INTERSECT",VERTEX,{"derivedFrom":[subQ0,sQuery(id+"F0.wireOp",EDGE,"E27")]});Q61=makeQuery(id+"F0.imprint","IMPRINT",FACE,{"disambiguationData":[TD([[makeQuery(id+"F0.imprint","IMPRINT",EDGE,{"disambiguationData":[TD([[subQ5,-1.0]])],"derivedFrom":subQ0}),-1.0]])]});}
            var Q62;
            {var subQ0=sQuery(id+"F0.wireOp",EDGE,"E8");var subQ5=makeQuery(id+"F0.imprint","INTERSECT",VERTEX,{"derivedFrom":[subQ0,sQuery(id+"F0.wireOp",EDGE,"E26")]});Q62=makeQuery(id+"F0.imprint","IMPRINT",FACE,{"disambiguationData":[TD([[makeQuery(id+"F0.imprint","IMPRINT",EDGE,{"disambiguationData":[TD([[subQ5,1.0]])],"derivedFrom":subQ0}),-1.0]])]});}
            var Q63;
            {var subQ0=sQuery(id+"F0.wireOp",EDGE,"E7");var subQ1=sQuery(id+"F0.wireOp",EDGE,"E2");var subQ2=makeQuery(id+"F0.imprint","INTERSECT",VERTEX,{"derivedFrom":[subQ1,subQ0]});Q63=makeQuery(id+"F0.imprint","IMPRINT",FACE,{"disambiguationData":[TD([[makeQuery(id+"F0.imprint","IMPRINT",EDGE,{"disambiguationData":[TD([[subQ2,-1.0]])],"derivedFrom":subQ1}),1.0]])]});}
            var Q64;
            {var subQ0=sQuery(id+"F0.wireOp",EDGE,"E7");var subQ1=sQuery(id+"F0.wireOp",EDGE,"E2");var subQ2=makeQuery(id+"F0.imprint","INTERSECT",VERTEX,{"derivedFrom":[subQ1,subQ0]});Q64=makeQuery(id+"F0.imprint","IMPRINT",FACE,{"disambiguationData":[TD([[makeQuery(id+"F0.imprint","IMPRINT",EDGE,{"disambiguationData":[TD([[subQ2,-1.0]])],"derivedFrom":subQ1}),-1.0]])]});}
            var Q65;
            {var subQ0=sQuery(id+"F0.wireOp",EDGE,"E9");var subQ1=sQuery(id+"F0.wireOp",EDGE,"E7");var subQ2=makeQuery(id+"F0.imprint","INTERSECT",VERTEX,{"derivedFrom":[subQ1,subQ0]});Q65=makeQuery(id+"F0.imprint","IMPRINT",FACE,{"disambiguationData":[TD([[makeQuery(id+"F0.imprint","IMPRINT",EDGE,{"disambiguationData":[TD([[subQ2,1.0]])],"derivedFrom":subQ1}),-1.0]])]});}
            var Q66;
            {var subQ0=sQuery(id+"F0.wireOp",EDGE,"E8");var subQ1=sQuery(id+"F0.wireOp",EDGE,"E7");var subQ2=makeQuery(id+"F0.imprint","INTERSECT",VERTEX,{"derivedFrom":[subQ1,subQ0]});Q66=makeQuery(id+"F0.imprint","IMPRINT",FACE,{"disambiguationData":[TD([[makeQuery(id+"F0.imprint","IMPRINT",EDGE,{"disambiguationData":[TD([[subQ2,-1.0]])],"derivedFrom":subQ1}),-1.0]])]});}
            var Q67;
            {var subQ0=sQuery(id+"F0.wireOp",EDGE,"E21");var subQ1=sQuery(id+"F0.wireOp",EDGE,"E7");var subQ2=makeQuery(id+"F0.imprint","INTERSECT",VERTEX,{"disambiguationData":[OD(0.0)],"derivedFrom":[subQ1,subQ0]});Q67=makeQuery(id+"F0.imprint","IMPRINT",FACE,{"disambiguationData":[TD([[makeQuery(id+"F0.imprint","IMPRINT",EDGE,{"disambiguationData":[TD([[subQ2,-1.0]])],"derivedFrom":subQ1}),-1.0]])]});}
            var Q68;
            {var subQ0=sQuery(id+"F0.wireOp",EDGE,"E42");var subQ1=sQuery(id+"F0.wireOp",EDGE,"E21");var subQ2=makeQuery(id+"F0.imprint","INTERSECT",VERTEX,{"disambiguationData":[OD(0.0)],"derivedFrom":[subQ1,subQ0]});Q68=makeQuery(id+"F0.imprint","IMPRINT",FACE,{"disambiguationData":[TD([[makeQuery(id+"F0.imprint","IMPRINT",EDGE,{"disambiguationData":[TD([[subQ2,-1.0]])],"derivedFrom":subQ1}),1.0]])]});}
            var Q69;
            {var subQ0=sQuery(id+"F0.wireOp",EDGE,"E21");var subQ1=sQuery(id+"F0.wireOp",EDGE,"E7");var subQ2=makeQuery(id+"F0.imprint","INTERSECT",VERTEX,{"disambiguationData":[OD(0.0)],"derivedFrom":[subQ1,subQ0]});Q69=makeQuery(id+"F0.imprint","IMPRINT",FACE,{"disambiguationData":[TD([[makeQuery(id+"F0.imprint","IMPRINT",EDGE,{"disambiguationData":[TD([[subQ2,-1.0]])],"derivedFrom":subQ1}),1.0]])]});}
            var Q70;
            {var subQ0=sQuery(id+"F0.wireOp",EDGE,"E44");var subQ1=sQuery(id+"F0.wireOp",EDGE,"E7");var subQ2=makeQuery(id+"F0.imprint","INTERSECT",VERTEX,{"disambiguationData":[OD(1.0)],"derivedFrom":[subQ1,subQ0]});Q70=makeQuery(id+"F0.imprint","IMPRINT",FACE,{"disambiguationData":[TD([[makeQuery(id+"F0.imprint","IMPRINT",EDGE,{"disambiguationData":[TD([[subQ2,-1.0]])],"derivedFrom":subQ1}),-1.0]])]});}
            var Q71;
            {var subQ3=sQuery(id+"F0.wireOp",EDGE,"E32");Q71=makeQuery(id+"F0.imprint","IMPRINT",FACE,{"disambiguationData":[TD([[makeQuery(id+"F0.imprint","IMPRINT",EDGE,{"derivedFrom":subQ3}),1.0]])]});}
            var Q72;
            {var subQ3=sQuery(id+"F0.wireOp",EDGE,"E33");Q72=makeQuery(id+"F0.imprint","IMPRINT",FACE,{"disambiguationData":[TD([[makeQuery(id+"F0.imprint","IMPRINT",EDGE,{"derivedFrom":subQ3}),-1.0]])]});}
            extrude(context, id + "F2", {"entities" : qUnion([Q0, Q1, Q2, Q3, Q4, Q5, Q6, Q7, Q8, Q9, Q10, Q11, Q12, Q13, Q14, Q15, Q16, Q17, Q18, Q19, Q20, Q21, Q22, Q23, Q24, Q25, Q26, Q27, Q28, Q29, Q30, Q31, Q32, Q33, Q34, Q35, Q36, Q37, Q38, Q39, Q40, Q41, Q42, Q43, Q44, Q45, Q46, Q47, Q48, Q49, Q50, Q51, Q52, Q53, Q54, Q55, Q56, Q57, Q58, Q59, Q60, Q61, Q62, Q63, Q64, Q65, Q66, Q67, Q68, Q69, Q70, Q71, Q72]), "depth" : 3.68 * mm});
        }
    });
